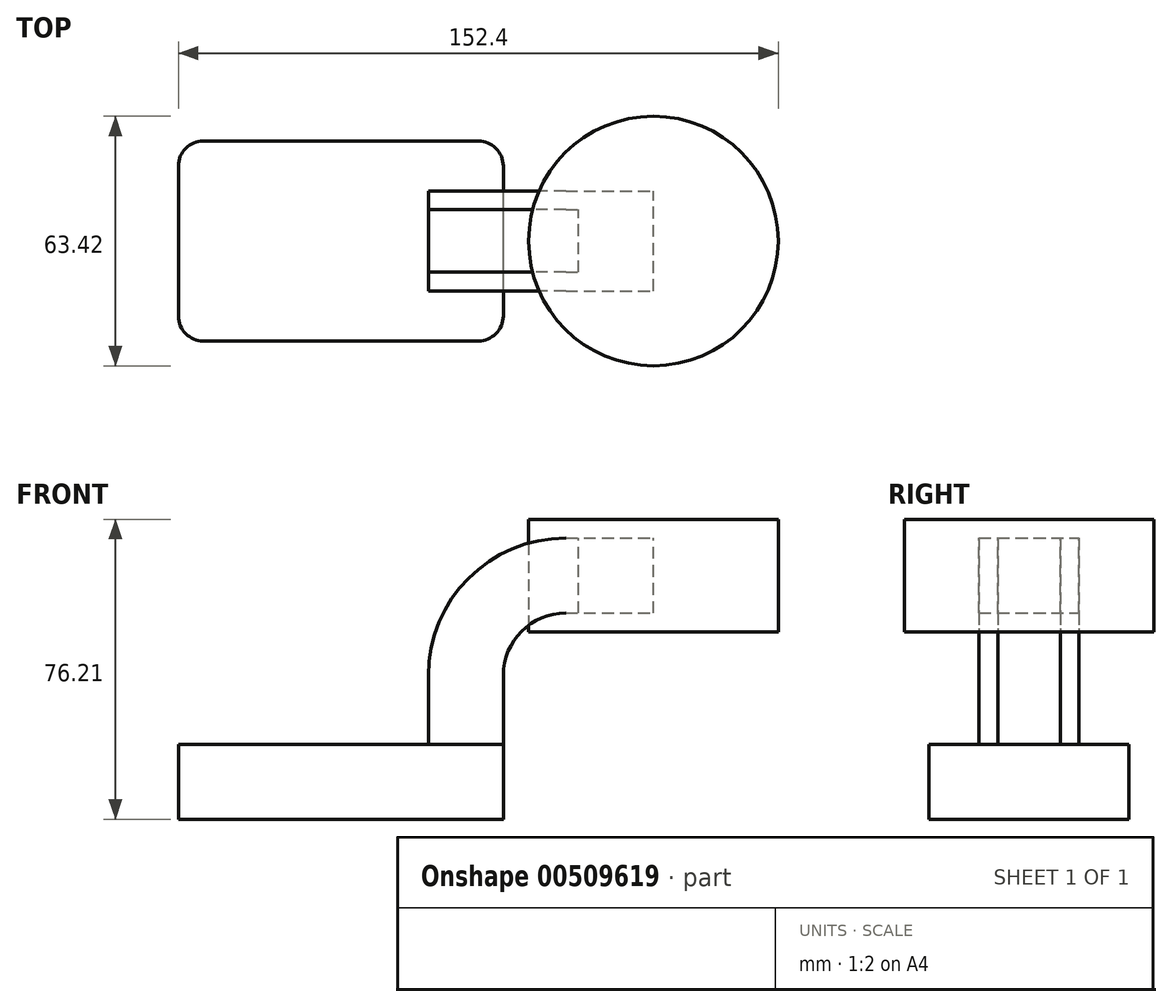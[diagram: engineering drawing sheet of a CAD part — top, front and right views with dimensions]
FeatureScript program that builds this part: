
annotation { "Feature Type Name" : "Feature", "Feature Type Description" : "" }
export const myFeature = defineFeature(function(context is Context, id is Id, definition is map)
    precondition{}
    {
        {
            var Q0;
            Q0=qCreatedBy(makeId("Front.planeOp"),FACE);
            var sketch = newSketch(context, id + "F0", { "sketchPlane" : qUnion([Q0])});
            skLineSegment(sketch, "E0.bottom", {"start": v(41.28, -9.52) * mm, "end": v(-41.27, -9.53) * mm});
            skLineSegment(sketch, "E0.top", {"start": v(41.27, 9.53) * mm, "end": v(-41.28, 9.53) * mm});
            skLineSegment(sketch, "E0.left", {"start": v(41.28, -9.52) * mm, "end": v(41.28, 9.53) * mm});
            skLineSegment(sketch, "E0.right", {"start": v(-41.27, -9.52) * mm, "end": v(-41.28, 9.53) * mm});
            skPoint(sketch, "E0.middle", {"position": v(0, 0) * mm});
            skLineSegment(sketch, "E1.bottom", {"start": v(111.12, 38.1) * mm, "end": v(60.32, 38.1) * mm});
            skLineSegment(sketch, "E1.top", {"start": v(111.12, 66.68) * mm, "end": v(60.32, 66.68) * mm});
            skLineSegment(sketch, "E1.left", {"start": v(111.12, 38.1) * mm, "end": v(111.12, 66.68) * mm});
            skLineSegment(sketch, "E1.right", {"start": v(60.32, 38.1) * mm, "end": v(60.32, 66.68) * mm});
            skPoint(sketch, "E1.middle", {"position": v(85.72, 52.39) * mm});
            skLineSegment(sketch, "E2", {"start": v(41.27, 9.53) * mm, "end": v(41.27, 27) * mm});
            skArc(sketch, "E3", {"start": v(41.27, 27) * mm, "mid": v(45.92, 38.23) * mm, "end": v(57.15, 42.88) * mm});
            skLineSegment(sketch, "E4", {"start": v(57.15, 42.88) * mm, "end": v(79.42, 42.88) * mm});
            skLineSegment(sketch, "E5.0", {"start": v(57.15, 61.93) * mm, "end": v(79.42, 61.93) * mm});
            skArc(sketch, "E5.1", {"start": v(22.23, 27) * mm, "mid": v(32.45, 51.7) * mm, "end": v(57.15, 61.93) * mm});
            skLineSegment(sketch, "E5.2", {"start": v(22.22, 9.53) * mm, "end": v(22.22, 27) * mm});
            skLineSegment(sketch, "E6", {"start": v(79.42, 38.1) * mm, "end": v(79.42, 66.68) * mm});
            skFitSpline(sketch, "E7", {"points": [v(-41.28, 9.52) * mm, v(57.15, 61.93) * mm], "startDerivative": vector(45.64, 111.19) * mm, "endDerivative": vector(132.74, 0.02) * mm});
            skSolve(sketch);
        }
        {
            var Q0;
            Q0=makeQuery(id+"F0.imprint","IMPRINT",FACE,{"disambiguationData":[TD([[makeQuery(id+"F0.imprint","IMPRINT",EDGE,{"derivedFrom":sQuery(id+"F0.wireOp",EDGE,"E5.1")}),1.0]])]});
            extrude(context, id + "F1", {"entities" : qUnion([Q0]), "endBound" : BoundingType.SYMMETRIC, "depth" : 15.88 * mm});
        }
        {
            var Q0;
            Q0=makeQuery(id+"F0.imprint","IMPRINT",FACE,{"disambiguationData":[TD([[makeQuery(id+"F0.imprint","IMPRINT",EDGE,{"derivedFrom":sQuery(id+"F0.wireOp",EDGE,"E0.bottom")}),-1.0]])]});
            extrude(context, id + "F2", {"entities" : qUnion([Q0]), "endBound" : BoundingType.SYMMETRIC, "depth" : 50.8 * mm});
        }
        {
            var Q0;
            {var subQ1=sQuery(id+"F0.wireOp",EDGE,"E2");Q0=makeQuery(id+"F0.imprint","IMPRINT",FACE,{"disambiguationData":[TD([[makeQuery(id+"F0.imprint","IMPRINT",EDGE,{"derivedFrom":subQ1}),1.0]])]});}
            var Q1;
            {var subQ0=sQuery(id+"F0.wireOp",EDGE,"E4");var subQ1=sQuery(id+"F0.wireOp",EDGE,"E1.right");var subQ2=makeQuery(id+"F0.imprint","INTERSECT",VERTEX,{"derivedFrom":[subQ1,subQ0]});Q1=makeQuery(id+"F0.imprint","IMPRINT",FACE,{"disambiguationData":[TD([[makeQuery(id+"F0.imprint","IMPRINT",EDGE,{"disambiguationData":[TD([[subQ2,-1.0]])],"derivedFrom":subQ1}),-1.0]])]});}
            extrude(context, id + "F3", {"entities" : qUnion([Q0, Q1]), "endBound" : BoundingType.SYMMETRIC, "depth" : 25.4 * mm});
        }
        {
            var Q0;
            {var subQ4=sQuery(id+"F0.wireOp",EDGE,"E1.left");Q0=makeQuery(id+"F0.imprint","IMPRINT",FACE,{"disambiguationData":[TD([[makeQuery(id+"F0.imprint","IMPRINT",EDGE,{"derivedFrom":subQ4}),1.0]])]});}
            var Q1;
            Q1=sQuery(id+"F0.wireOp",EDGE,"E6");
            revolve(context, id + "F4", {"entities" : qUnion([Q0]), "axis" : qUnion([Q1]), "revolveType" : RevolveType.FULL});
        }
        {
            var Q0;
            Q0=makeQuery(id+"F2.opExtrude","CAP_EDGE",EDGE,{"disambiguationData":[OSD([sQuery(id+"F0.wireOp",EDGE,"E0.right")])],"isStart":false});
            var Q1;
            Q1=makeQuery(id+"F2.opExtrude","CAP_EDGE",EDGE,{"disambiguationData":[OSD([sQuery(id+"F0.wireOp",EDGE,"E0.left")])],"isStart":false});
            var Q2;
            Q2=makeQuery(id+"F2.opExtrude","CAP_EDGE",EDGE,{"disambiguationData":[OSD([sQuery(id+"F0.wireOp",EDGE,"E0.left")])],"isStart":true});
            var Q3;
            Q3=makeQuery(id+"F2.opExtrude","CAP_EDGE",EDGE,{"disambiguationData":[OSD([sQuery(id+"F0.wireOp",EDGE,"E0.right")])],"isStart":true});
            fillet(context, id + "F5", {"entities" : qUnion([Q0, Q1, Q2, Q3]), "radius" : 6.35 * mm, "tangentPropagation" : true, "allowEdgeOverflow" : false});
        }
    });
